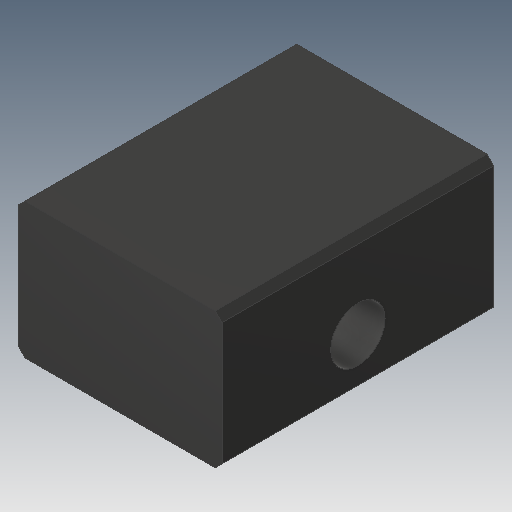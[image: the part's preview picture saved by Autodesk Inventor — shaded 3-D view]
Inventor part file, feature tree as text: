
AUTODESK INVENTOR PART (.ipt)
format: ipt  version: 2018 (Build 220112000, 112)  size: 98,816 bytes
history: native  units: in
note: dims shown in document units (in); Inventor stores cm internally (conversion verified against a paired STEP export)
features: other x3, sketch x1
ambient origin geometry x8: Origin, YZ Plane, XZ Plane, XY Plane, X Axis, Y Axis, Z Axis, Center Point
bodies: Solid1 (feature_tree)
feature tree (4):
  other  "10-006-ACTR-FIX.ipt"
  other  "Solid1::10-006-ACTR-FIX.ipt"
  other  "TaggingFeature1"
  sketch  "Sketch1"  dims[d0=0.3937in]
